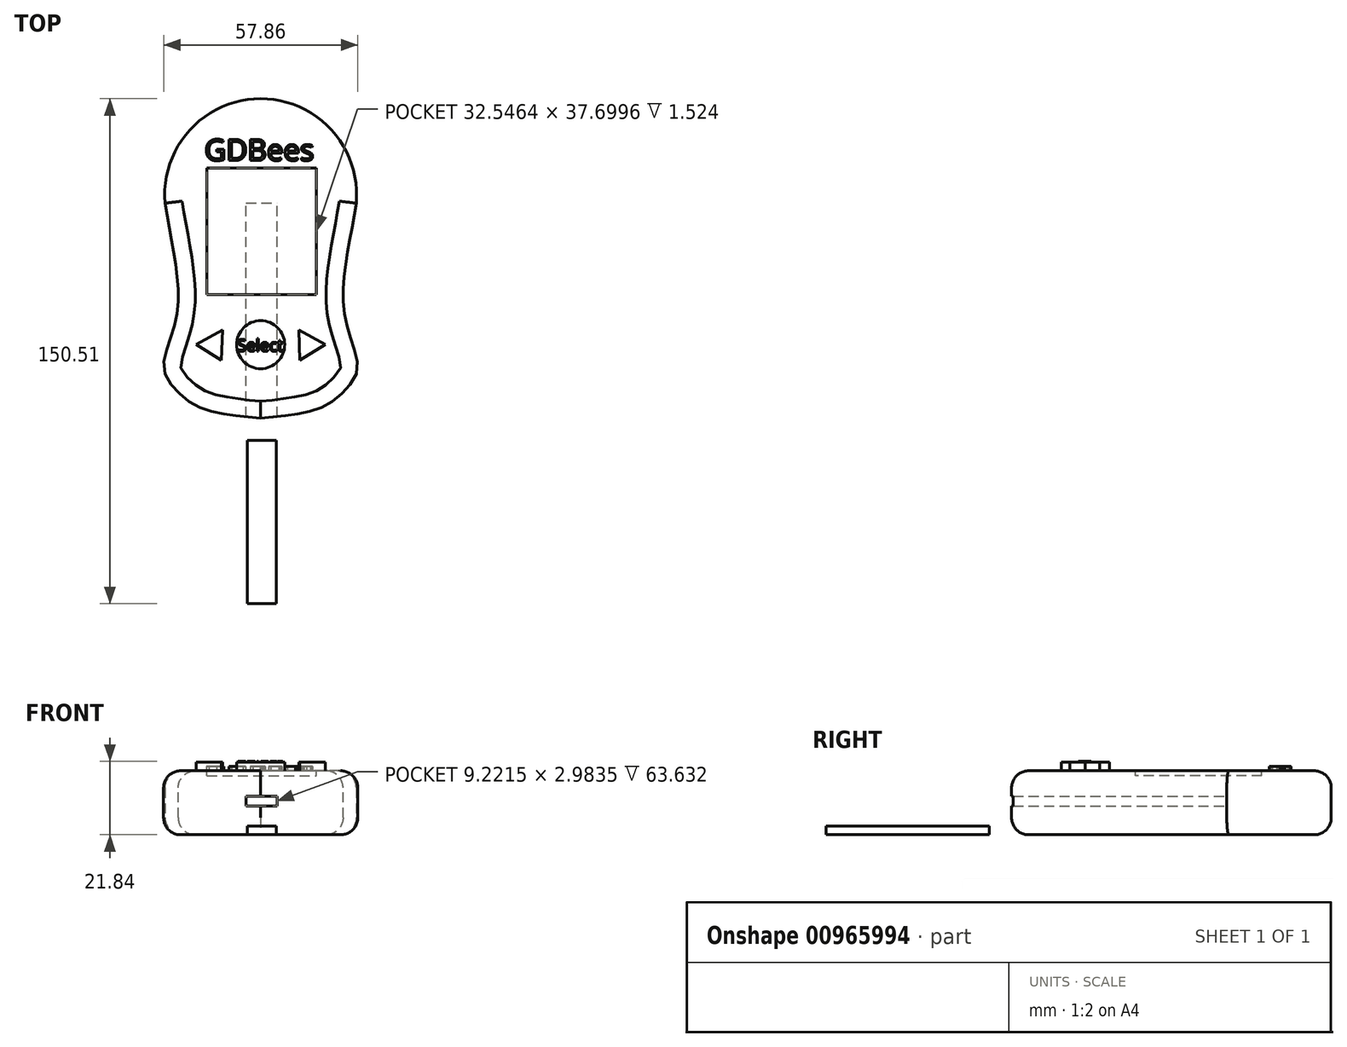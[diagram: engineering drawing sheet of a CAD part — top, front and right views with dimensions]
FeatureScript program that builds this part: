
annotation { "Feature Type Name" : "Feature", "Feature Type Description" : "" }
export const myFeature = defineFeature(function(context is Context, id is Id, definition is map)
    precondition{}
    {
        {
            var Q0;
            Q0=qCreatedBy(makeId("Top.planeOp"),FACE);
            var sketch = newSketch(context, id + "F0", { "sketchPlane" : qUnion([Q0])});
            skArc(sketch, "E0", {"start": v(28.48, 0) * mm, "mid": v(0, 31.14) * mm, "end": v(-28.48, 0) * mm});
            skFitSpline(sketch, "E1", {"points": [v(-28.48, 0) * mm, v(-24.68, -30.51) * mm, v(-28.48, -45.43) * mm, v(-28.48, -51.13) * mm, v(-24.68, -56.28) * mm, v(-17.36, -61.16) * mm, v(0, -64.14) * mm], "startDerivative": vector(19.49, -126.18) * mm, "endDerivative": vector(97.46, -9.91) * mm});
            skFitSpline(sketch, "E2.MirrorCS", {"points": [v(28.48, 0) * mm, v(24.68, -30.51) * mm, v(28.48, -45.43) * mm, v(28.48, -51.13) * mm, v(24.68, -56.28) * mm, v(17.36, -61.16) * mm, v(0, -64.14) * mm], "startDerivative": vector(-19.49, -126.18) * mm, "endDerivative": vector(-97.46, -9.91) * mm});
            skSolve(sketch);
        }
        {
            var Q0;
            Q0=makeQuery(id+"F0.imprint","IMPRINT",FACE,{"disambiguationData":[TD([[makeQuery(id+"F0.imprint","IMPRINT",EDGE,{"derivedFrom":sQuery(id+"F0.wireOp",EDGE,"E0")}),1.0]])]});
            extrude(context, id + "F1", {"entities" : qUnion([Q0]), "depth" : 19.05 * mm, "offsetDistance" : 25.4 * mm});
        }
        {
            var Q0;
            Q0=makeQuery(id+"F1.opExtrude","CAP_EDGE",EDGE,{"disambiguationData":[OSD([sQuery(id+"F0.wireOp",EDGE,"E2.MirrorCS")])],"isStart":false});
            var Q1;
            Q1=makeQuery(id+"F1.opExtrude","CAP_EDGE",EDGE,{"disambiguationData":[OSD([sQuery(id+"F0.wireOp",EDGE,"E1")])],"isStart":false});
            var Q2;
            Q2=makeQuery(id+"F1.opExtrude","CAP_EDGE",EDGE,{"disambiguationData":[OSD([sQuery(id+"F0.wireOp",EDGE,"E0")])],"isStart":false});
            var Q3;
            Q3=makeQuery(id+"F1.opExtrude","CAP_EDGE",EDGE,{"disambiguationData":[OSD([sQuery(id+"F0.wireOp",EDGE,"E2.MirrorCS")])],"isStart":true});
            var Q4;
            Q4=makeQuery(id+"F1.opExtrude","CAP_EDGE",EDGE,{"disambiguationData":[OSD([sQuery(id+"F0.wireOp",EDGE,"E0")])],"isStart":true});
            var Q5;
            Q5=makeQuery(id+"F1.opExtrude","CAP_EDGE",EDGE,{"disambiguationData":[OSD([sQuery(id+"F0.wireOp",EDGE,"E1")])],"isStart":true});
            fillet(context, id + "F2", {"entities" : qUnion([Q0, Q1, Q2, Q3, Q4, Q5]), "radius" : 5.08 * mm, "tangentPropagation" : true, "allowEdgeOverflow" : false});
        }
        {
            var Q0;
            Q0=makeQuery(id+"F1.opExtrude","CAP_FACE",FACE,{"disambiguationData":[OSD([sQuery(id+"F0.wireOp",EDGE,"E0"),sQuery(id+"F0.wireOp",EDGE,"E1"),sQuery(id+"F0.wireOp",EDGE,"E2.MirrorCS")])],"isStart":false});
            var sketch = newSketch(context, id + "F3", { "sketchPlane" : qUnion([Q0])});
            skLineSegment(sketch, "E3.bottom", {"start": v(-16, 10.44) * mm, "end": v(16.54, 10.44) * mm});
            skLineSegment(sketch, "E3.top", {"start": v(-16, -27.26) * mm, "end": v(16.54, -27.26) * mm});
            skLineSegment(sketch, "E3.left", {"start": v(-16, 10.44) * mm, "end": v(-16, -27.26) * mm});
            skLineSegment(sketch, "E3.right", {"start": v(16.54, 10.44) * mm, "end": v(16.54, -27.26) * mm});
            skSolve(sketch);
        }
        {
            var Q0;
            Q0=makeQuery(id+"F3.imprint","IMPRINT",FACE,{"disambiguationData":[TD([[makeQuery(id+"F3.imprint","IMPRINT",EDGE,{"derivedFrom":sQuery(id+"F3.wireOp",EDGE,"E3.bottom")}),-1.0]])]});
            extrude(context, id + "F4", {"entities" : qUnion([Q0]), "operationType" : NewBodyOperationType.REMOVE, "oppositeDirection" : true, "depth" : 1.52 * mm, "offsetDistance" : 25.4 * mm});
        }
        {
            var Q0;
            Q0=makeQuery(id+"F1.opExtrude","CAP_FACE",FACE,{"disambiguationData":[OSD([sQuery(id+"F0.wireOp",EDGE,"E0"),sQuery(id+"F0.wireOp",EDGE,"E1"),sQuery(id+"F0.wireOp",EDGE,"E2.MirrorCS")])],"isStart":false});
            var sketch = newSketch(context, id + "F5", { "sketchPlane" : qUnion([Q0])});
            skLineSegment(sketch, "E4", {"start": v(-11.4, -37.84) * mm, "end": v(-19.26, -42.17) * mm});
            skLineSegment(sketch, "E5", {"start": v(-19.26, -42.17) * mm, "end": v(-11.66, -46.79) * mm});
            skLineSegment(sketch, "E6", {"start": v(-11.66, -46.79) * mm, "end": v(-11.4, -37.84) * mm});
            skLineSegment(sketch, "E7.MirrorCS", {"start": v(19.26, -42.17) * mm, "end": v(11.66, -46.79) * mm});
            skLineSegment(sketch, "E8.MirrorCS", {"start": v(11.4, -37.84) * mm, "end": v(19.26, -42.17) * mm});
            skLineSegment(sketch, "E9.MirrorCS", {"start": v(11.66, -46.79) * mm, "end": v(11.4, -37.84) * mm});
            skSolve(sketch);
        }
        {
            var Q0;
            Q0=makeQuery(id+"F5.imprint","IMPRINT",FACE,{"disambiguationData":[TD([[makeQuery(id+"F5.imprint","IMPRINT",EDGE,{"derivedFrom":sQuery(id+"F5.wireOp",EDGE,"E4")}),1.0]])]});
            var Q1;
            Q1=makeQuery(id+"F5.imprint","IMPRINT",FACE,{"disambiguationData":[TD([[makeQuery(id+"F5.imprint","IMPRINT",EDGE,{"derivedFrom":sQuery(id+"F5.wireOp",EDGE,"E7.MirrorCS")}),-1.0]])]});
            extrude(context, id + "F6", {"entities" : qUnion([Q0, Q1]), "operationType" : NewBodyOperationType.ADD, "depth" : 2.54 * mm, "offsetDistance" : 25.4 * mm});
        }
        {
            var Q0;
            Q0=makeQuery(id+"F1.opExtrude","CAP_FACE",FACE,{"disambiguationData":[OSD([sQuery(id+"F0.wireOp",EDGE,"E0"),sQuery(id+"F0.wireOp",EDGE,"E1"),sQuery(id+"F0.wireOp",EDGE,"E2.MirrorCS")])],"isStart":false});
            var sketch = newSketch(context, id + "F7", { "sketchPlane" : qUnion([Q0])});
            skCircle(sketch, "E10", {"center": v(0, -42.17) * mm, "radius": 7.16 * mm});
            skSolve(sketch);
        }
        {
            var Q0;
            Q0=makeQuery(id+"F7.imprint","IMPRINT",FACE,{"disambiguationData":[TD([[makeQuery(id+"F7.imprint","IMPRINT",EDGE,{"derivedFrom":sQuery(id+"F7.wireOp",EDGE,"E10")}),1.0]])]});
            extrude(context, id + "F8", {"entities" : qUnion([Q0]), "operationType" : NewBodyOperationType.ADD, "depth" : 2.54 * mm, "offsetDistance" : 25.4 * mm});
        }
        {
            var Q0;
            Q0=qCreatedBy(makeId("Top.planeOp"),FACE);
            var sketch = newSketch(context, id + "F9", { "sketchPlane" : qUnion([Q0])});
            skLineSegment(sketch, "E11.bottom", {"start": v(-3.94, -70.72) * mm, "end": v(4.67, -70.72) * mm});
            skLineSegment(sketch, "E11.top", {"start": v(-3.94, -119.37) * mm, "end": v(4.67, -119.37) * mm});
            skLineSegment(sketch, "E11.left", {"start": v(-3.94, -70.72) * mm, "end": v(-3.94, -119.37) * mm});
            skLineSegment(sketch, "E11.right", {"start": v(4.67, -70.72) * mm, "end": v(4.67, -119.37) * mm});
            skSolve(sketch);
        }
        {
            var Q0;
            Q0=makeQuery(id+"F9.imprint","IMPRINT",FACE,{"disambiguationData":[TD([[makeQuery(id+"F9.imprint","IMPRINT",EDGE,{"derivedFrom":sQuery(id+"F9.wireOp",EDGE,"E11.bottom")}),-1.0]])]});
            extrude(context, id + "F10", {"entities" : qUnion([Q0]), "depth" : 2.54 * mm, "offsetDistance" : 25.4 * mm});
        }
        {
            var Q0;
            Q0=qCreatedBy(makeId("Front.planeOp"),FACE);
            var sketch = newSketch(context, id + "F11", { "sketchPlane" : qUnion([Q0])});
            skLineSegment(sketch, "E12.bottom", {"start": v(-4.34, 11.53) * mm, "end": v(4.88, 11.53) * mm});
            skLineSegment(sketch, "E12.top", {"start": v(-4.34, 8.54) * mm, "end": v(4.88, 8.54) * mm});
            skLineSegment(sketch, "E12.left", {"start": v(-4.34, 11.53) * mm, "end": v(-4.34, 8.54) * mm});
            skLineSegment(sketch, "E12.right", {"start": v(4.88, 11.53) * mm, "end": v(4.88, 8.54) * mm});
            skSolve(sketch);
        }
        {
            var Q0;
            Q0 = qSketchRegion(id + "F11", true);
            extrude(context, id + "F12", {"entities" : qUnion([Q0]), "operationType" : NewBodyOperationType.REMOVE, "depth" : 188.47 * mm, "offsetDistance" : 25.4 * mm});
        }
        {
            var Q0;
            Q0=makeQuery(id+"F1.opExtrude","CAP_FACE",FACE,{"disambiguationData":[OSD([sQuery(id+"F0.wireOp",EDGE,"E0"),sQuery(id+"F0.wireOp",EDGE,"E1"),sQuery(id+"F0.wireOp",EDGE,"E2.MirrorCS")])],"isStart":false});
            var sketch = newSketch(context, id + "F13", { "sketchPlane" : qUnion([Q0])});
            skText(sketch, "E13", { "text": "GDBees", "fontName": "OpenSans-Regular.ttf"});
            const initialGuessF13  = {"E13": [-0.01675, 0.0127, 1, 0, 0.00635]};
            skSetInitialGuess(sketch, initialGuessF13);
            skSolve(sketch);
        }
        {
            var Q0;
            Q0 = qSketchRegion(id + "F13", true);
            extrude(context, id + "F14", {"entities" : qUnion([Q0]), "operationType" : NewBodyOperationType.ADD, "depth" : 1.27 * mm, "offsetDistance" : 25.4 * mm});
        }
        {
            var Q0;
            Q0=makeQuery(id+"F8.opExtrude","CAP_FACE",FACE,{"disambiguationData":[OSD([sQuery(id+"F7.wireOp",EDGE,"E10")])],"isStart":false});
            var sketch = newSketch(context, id + "F15", { "sketchPlane" : qUnion([Q0])});
            skText(sketch, "E14", { "text": "Select", "fontName": "OpenSans-Regular.ttf"});
            const initialGuessF15  = {"E14": [-0.00698, -0.04414, 1, 0, 0.00357]};
            skSetInitialGuess(sketch, initialGuessF15);
            skSolve(sketch);
        }
        {
            var Q0;
            Q0 = qSketchRegion(id + "F15", true);
            extrude(context, id + "F16", {"entities" : qUnion([Q0]), "operationType" : NewBodyOperationType.ADD, "depth" : 0.25 * mm, "offsetDistance" : 25.4 * mm});
        }
    });
